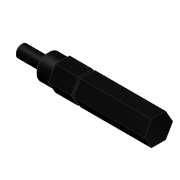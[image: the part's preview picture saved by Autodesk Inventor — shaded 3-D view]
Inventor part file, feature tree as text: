
AUTODESK INVENTOR PART (.ipt)
format: ipt  version: 2012 (Build 160160000, 160)  size: 103,424 bytes
history: native  units: in
note: dims shown in document units (in); Inventor stores cm internally (conversion verified against a paired STEP export)
features: other x2, extrude x1, imported_body x1, sketch x1
ambient origin geometry x8: Origin, YZ Plane, XZ Plane, XY Plane, X Axis, Y Axis, Z Axis, Center Point
feature tree (5):
  other  "Cut-Revolve3"
  other  "217-2454-004 Rev11"
  extrude  "Extrusion1"  Depth=2.75in TaperAngle=0.0deg
  imported_body  "Base1"
  sketch  "Sketch1"  dims[d0=0.5in d1=2.75in d2=0.0in]
